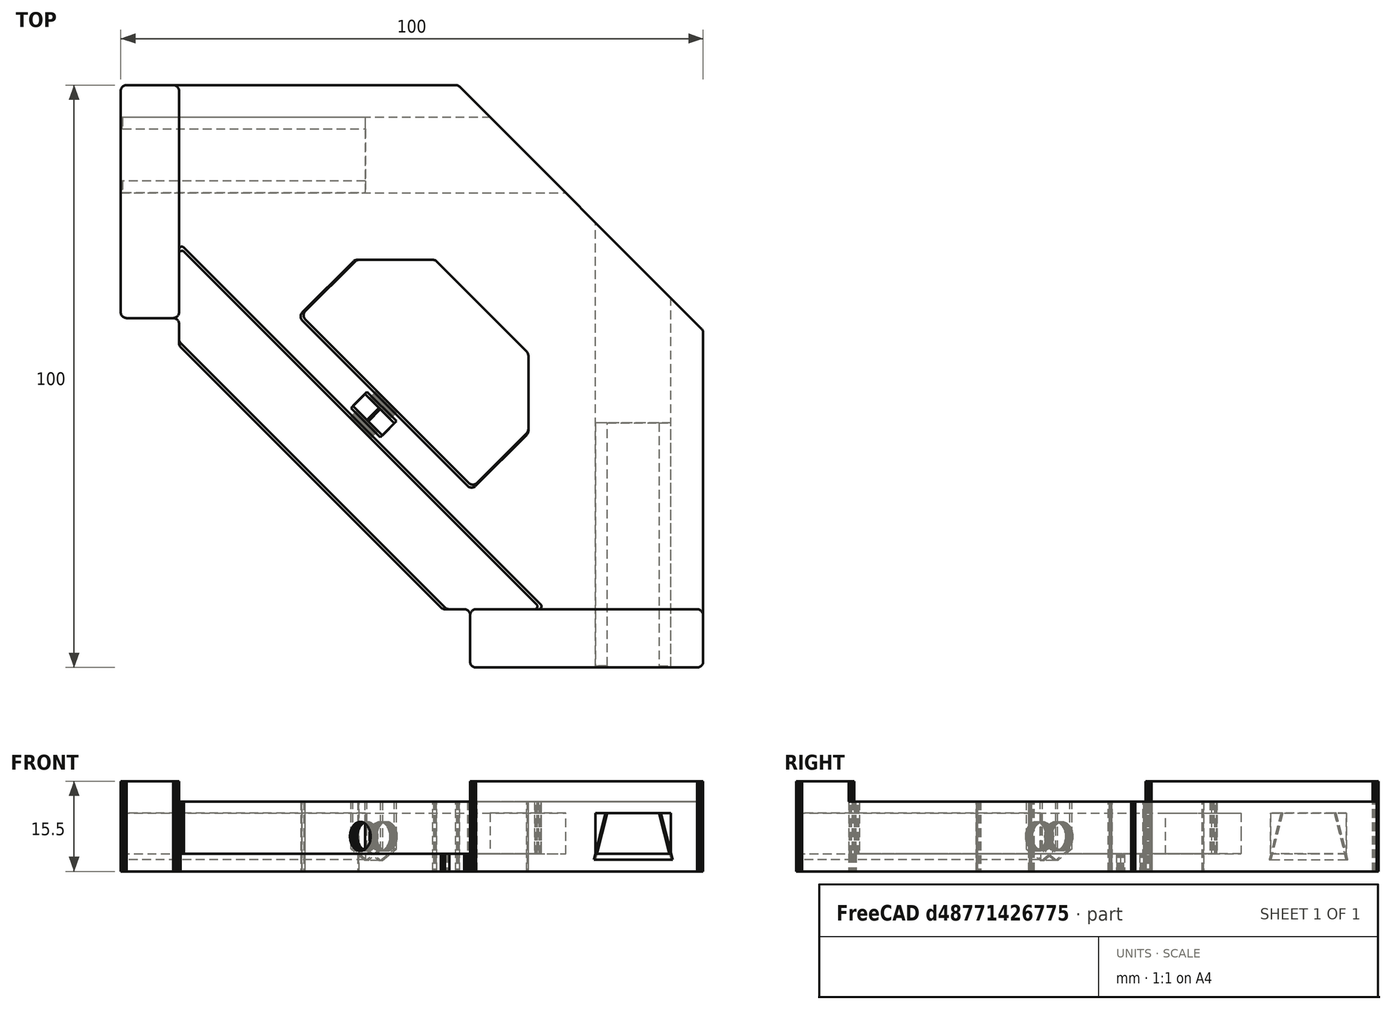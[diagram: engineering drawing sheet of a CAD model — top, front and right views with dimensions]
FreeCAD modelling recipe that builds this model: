
FCSTD DOCUMENT  (FreeCAD 0.20RUnknown)
Label: RouterTemplate
License: All rights reserved
LicenseURL: http://en.wikipedia.org/wiki/All_rights_reserved
objects: Part::Feature×4, Sketcher::SketchObject×4, Mesh::Feature×2, PartDesign::Pad×2, PartDesign::Pocket×2, PartDesign::FeatureBase×1, PartDesign::Body×1
note: 18 computed .brp shape members not serialized (recipe doc carries the construction recipe); baked Part::Feature solids carry a one-line shape summary decoded from their .brp

FEATURE [Mesh::Feature] Fr__sschablone  label="Frässchablone"
FEATURE [Part::Feature] Fr__sschablone001  label="Fraesschablone001"
  shape: bbox 100 x 100 x 15.5 mm, 1928 faces, 0 solids (baked)
FEATURE [Part::Feature] Fr__sschablone001_solid  label="Fraesschablone001 (Solid)"
  shape: bbox 100 x 100 x 15.5 mm, 1928 faces (baked)
FEATURE [Sketcher::SketchObject] Sketch003
  FullyConstrained = false
  MapMode = 5
  Placement = pos=(-1e-15,0,0) rot=(0.57735,-0.57735,-0.57735;2.0944rad)
  sketch-geometry (4):
    g0: LineSegment StartX=-79.4162 StartY=1.23591 StartZ=0 EndX=-95.1419 EndY=1.23591 EndZ=0
    g1: LineSegment StartX=-95.1419 StartY=1.23591 StartZ=0 EndX=-95.1419 EndY=10.2098 EndZ=0
    g2: LineSegment StartX=-95.1419 StartY=10.2098 StartZ=0 EndX=-79.4162 EndY=10.2098 EndZ=0
    g3: LineSegment StartX=-79.4162 StartY=10.2098 StartZ=0 EndX=-79.4162 EndY=1.23591 EndZ=0
  constraints (8):
    c: Coincident(g0,g1)
    c: Coincident(g1,g2)
    c: Coincident(g2,g3)
    c: Coincident(g3,g0)
    c: Horizontal(g0)
    c: Horizontal(g2)
    c: Vertical(g1)
    c: Vertical(g3)
FEATURE [Mesh::Feature] Fr__sschablone_reduced_clearance  label="Frässchablone_reduced_clearance"
FEATURE [Part::Feature] Fr__sschablone_reduced_clearance001  label="Fraesschablone_reduced_clearance"
  shape: bbox 100 x 100 x 15.5 mm, 1928 faces, 0 solids (baked)
FEATURE [Part::Feature] Fr__sschablone_reduced_clearance001_solid  label="Fraesschablone_reduced_clearance (Solid)"
  shape: bbox 100 x 100 x 15.5 mm, 1928 faces (baked)
FEATURE [PartDesign::FeatureBase] BaseFeature
  BaseFeature = -> Fr__sschablone_reduced_clearance001_solid
FEATURE [Sketcher::SketchObject] Sketch001
  FullyConstrained = false
  MapMode = 5
  Placement = pos=(0,-8.9e-15,0) rot=(1,0,0;1.5708rad)
  Support = -> [BaseFeature]
  sketch-geometry (4):
    g0: LineSegment StartX=78.7622 StartY=11.1825 StartZ=0 EndX=96.5942 EndY=11.1825 EndZ=0
    g1: LineSegment StartX=96.5942 StartY=11.1825 StartZ=0 EndX=96.5942 EndY=1.22974 EndZ=0
    g2: LineSegment StartX=96.5942 StartY=1.22974 StartZ=0 EndX=78.7622 EndY=1.22974 EndZ=0
    g3: LineSegment StartX=78.7622 StartY=1.22974 StartZ=0 EndX=78.7622 EndY=11.1825 EndZ=0
  constraints (8):
    c: Coincident(g0,g1)
    c: Coincident(g1,g2)
    c: Coincident(g2,g3)
    c: Coincident(g3,g0)
    c: Horizontal(g0)
    c: Horizontal(g2)
    c: Vertical(g1)
    c: Vertical(g3)
FEATURE [PartDesign::Pad] Pad  label="DeChamferPad"
  BaseFeature = -> BaseFeature
  Direction = (1e-16,-1,2e-16)
  Length = 10
  Length2 = 10
  Profile = -> Sketch001
  ReferenceAxis = -> Sketch001 [N_Axis]
  Reversed = true
  Type = 1
FEATURE [PartDesign::Pad] Pad001  label="DeChamferPad001"
  BaseFeature = -> Pad
  Direction = (-1,0,0)
  Length = 10
  Length2 = 10
  Profile = -> Sketch003
  ReferenceAxis = -> Sketch003 [N_Axis]
  Reversed = true
  Type = 1
FEATURE [Sketcher::SketchObject] Sketch
  ExternalGeometry = -> [BaseFeature]
  FullyConstrained = true
  MapMode = 5
  Placement = pos=(-6e-16,0,0) rot=(-0.57735,0.57735,0.57735;4.18879rad)
  Support = -> [BaseFeature]
  expr: Constraints[8] = 6 + 1
  expr: Constraints[9] = 12 + 1
  sketch-geometry (6):
    g0: LineSegment StartX=-94.5 StartY=10 StartZ=0 EndX=-81.5 EndY=10 EndZ=0
    g1: LineSegment StartX=-81.5 StartY=10 StartZ=0 EndX=-81.5 EndY=3 EndZ=0
    g2: LineSegment StartX=-81.5 StartY=3 StartZ=0 EndX=-94.5 EndY=3 EndZ=0
    g3: LineSegment StartX=-94.5 StartY=3 StartZ=0 EndX=-94.5 EndY=10 EndZ=0
    g4: LineSegment StartX=-92.4554 StartY=10 StartZ=0 EndX=-88 EndY=10 EndZ=0
    g5: LineSegment StartX=-88 StartY=10 StartZ=0 EndX=-83.5446 EndY=10 EndZ=0
  constraints (16):
    c: Coincident(g0,g1)
    c: Coincident(g1,g2)
    c: Coincident(g2,g3)
    c: Coincident(g3,g0)
    c: Horizontal(g0)
    c: Horizontal(g2)
    c: Vertical(g1)
    c: Vertical(g3)
    c: DistanceY(g1,g1) = 7
    c: DistanceX(g2,g2) = 13
    c: Coincident(g4,g-3)
    c: Coincident(g5,g-3)
    c: Coincident(g4,g5)
    c: Equal(g4,g5)
    c: Symmetric(g0,g0,g4)
    c: Horizontal(g4)
FEATURE [Sketcher::SketchObject] Sketch004
  ExternalGeometry = -> [BaseFeature]
  FullyConstrained = true
  MapMode = 5
  Placement = pos=(0,-8.9e-15,0) rot=(1,0,0;1.5708rad)
  Support = -> [BaseFeature]
  expr: Constraints[13] = 6 + 1
  expr: Constraints[14] = 12 + 1
  sketch-geometry (6):
    g0: LineSegment StartX=83.5446 StartY=10 StartZ=0 EndX=88 EndY=10 EndZ=0
    g1: LineSegment StartX=88 StartY=10 StartZ=0 EndX=92.4554 EndY=10 EndZ=0
    g2: LineSegment StartX=81.5 StartY=10 StartZ=0 EndX=94.5 EndY=10 EndZ=0
    g3: LineSegment StartX=94.5 StartY=10 StartZ=0 EndX=94.5 EndY=3 EndZ=0
    g4: LineSegment StartX=94.5 StartY=3 StartZ=0 EndX=81.5 EndY=3 EndZ=0
    g5: LineSegment StartX=81.5 StartY=3 StartZ=0 EndX=81.5 EndY=10 EndZ=0
  constraints (16):
    c: Coincident(g0,g-3)
    c: Coincident(g1,g-3)
    c: Coincident(g0,g1)
    c: Equal(g0,g1)
    c: Horizontal(g0)
    c: Coincident(g2,g3)
    c: Coincident(g3,g4)
    c: Coincident(g4,g5)
    c: Coincident(g5,g2)
    c: Horizontal(g2)
    c: Horizontal(g4)
    c: Vertical(g3)
    c: Vertical(g5)
    c: DistanceY(g3,g3) = 7
    c: DistanceX(g4,g4) = 13
    c: Symmetric(g2,g2,g0)
FEATURE [PartDesign::Pocket] Pocket
  BaseFeature = -> Pad001
  Direction = (1,0,0)
  Length = 5
  Length2 = 5
  Profile = -> Sketch
  ReferenceAxis = -> Sketch [N_Axis]
  Type = 1
FEATURE [PartDesign::Pocket] Pocket001
  BaseFeature = -> Pocket
  Direction = (-1e-16,1,-2e-16)
  Length = 5
  Length2 = 5
  Profile = -> Sketch004
  ReferenceAxis = -> Sketch004 [N_Axis]
  Type = 1
FEATURE [PartDesign::Body] Body
  BaseFeature = -> Fr__sschablone_reduced_clearance001_solid
  Group = -> [BaseFeature,Sketch001,Pad,Sketch003,Pad001,Sketch,Sketch004,Pocket,Pocket001]
  Origin = -> Origin
  Tip = -> Pocket001
